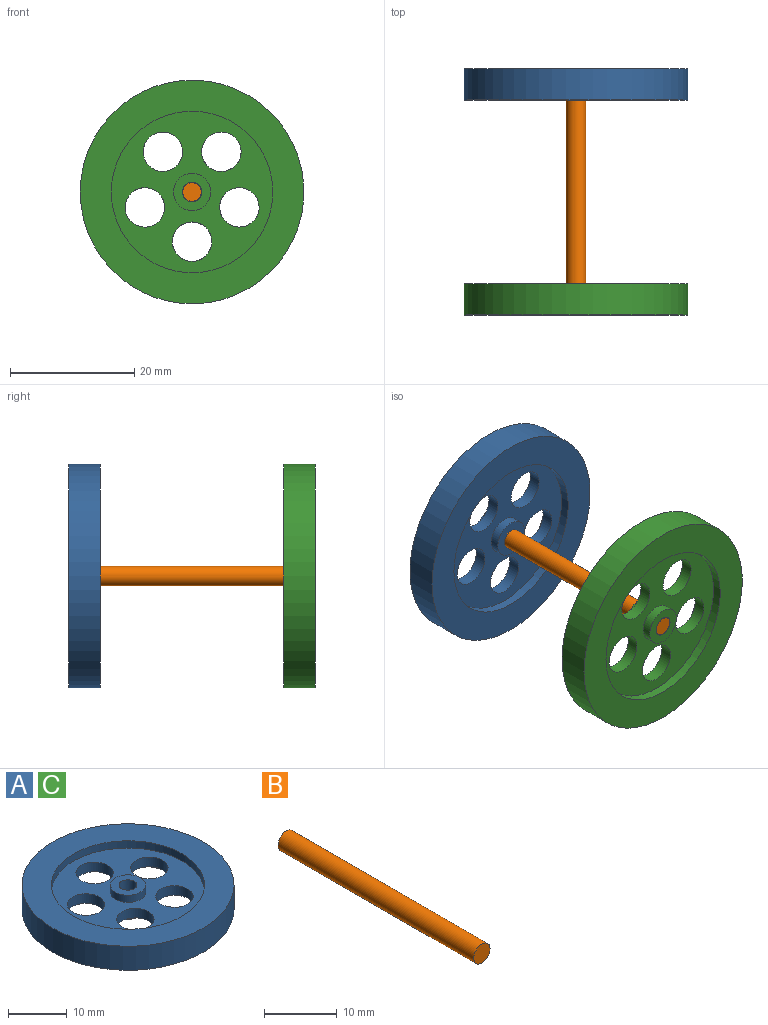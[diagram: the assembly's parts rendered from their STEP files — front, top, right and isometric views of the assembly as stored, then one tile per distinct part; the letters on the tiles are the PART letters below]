
ASSEMBLY  parts=3 mates=1
PART A: 17 faces, bbox 36x36x5 mm
  f0: cylinder r=18mm len=36mm, axis (0,0,-1), area 565.5mm2, adj f1,f10
  f1: plane 36x36mm, normal (0,0,1), area 486.9mm2, adj f0,f2
  f2: cylinder r=13mm len=26mm, axis (0,0,-1), area 122.5mm2, adj f1,f3
  f3: plane 26x26mm, normal (0,0,1), area 344.3mm2, adj f2,f4,f12,f13,f14,f15,f16
  f4: cylinder r=3mm len=6mm, axis (0,0,-1), area 28.3mm2, adj f3,f5
  f5: plane 6x6mm, normal (0,0,1), area 21.2mm2, adj f4,f11
  f6: plane 6x6mm, normal (0,0,-1), area 21.2mm2, adj f7,f11
  f7: cylinder r=3mm len=6mm, axis (0,0,-1), area 28.3mm2, adj f6,f8
  f8: plane 26x26mm, normal (0,0,-1), area 344.3mm2, adj f7,f9,f12,f13,f14,f15,f16
  f9: cylinder r=13mm len=26mm, axis (0,0,-1), area 122.5mm2, adj f8,f10
  f10: plane 36x36mm, normal (0,0,-1), area 486.9mm2, adj f0,f9
  f11: cylinder r=1.5mm len=5mm, axis (0,0,-1), area 47.1mm2, adj f5,f6
  f12: cylinder r=3.17mm len=6.35mm, axis (0,0,1), area 39.9mm2, adj f3,f8
  f13: cylinder r=3.17mm len=6.35mm, axis (0,0,1), area 39.9mm2, adj f3,f8
  f14: cylinder r=3.17mm len=6.35mm, axis (0,0,1), area 39.9mm2, adj f3,f8
  f15: cylinder r=3.17mm len=6.35mm, axis (0,0,1), area 39.9mm2, adj f3,f8
  f16: cylinder r=3.17mm len=6.35mm, axis (0,0,1), area 39.9mm2, adj f3,f8
PART B: 3 faces, bbox 3.2x38.1x3.2 mm
  f0: cylinder r=1.59mm len=38.1mm, axis (0,1,0), area 380mm2, adj f1,f2
  f1: plane 3.18x3.18mm, normal (0,-1,0), area 7.9mm2, adj f0
  f2: plane 3.18x3.18mm, normal (0,1,0), area 7.9mm2, adj f0
PART C: same geometry as A
PLACE A rot(axis=(-1,0,0),90deg) t=(-27.37,0.26,-2.98)mm
PLACE B t=(-3.19,1.26,-2.98)mm fixed
PLACE C rot(axis=(-1,0,0),90deg) t=(-27.37,-34.34,-2.98)mm
MATE fastened B.f0 <-> A.f0  axis (0,1,0) through (-27.37,1.26,-2.98)mm
